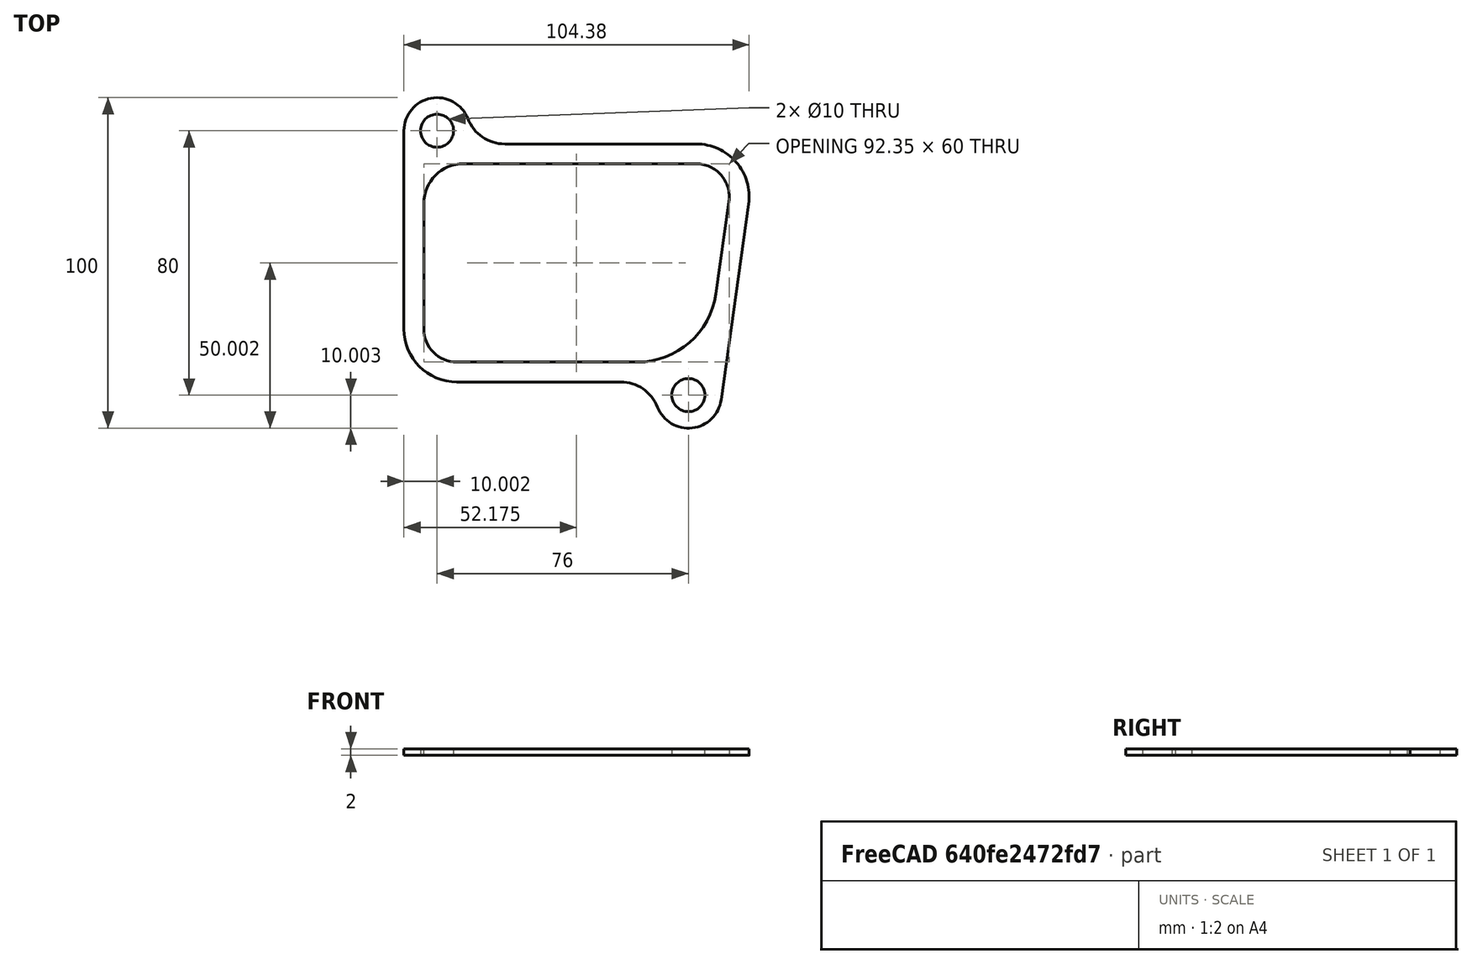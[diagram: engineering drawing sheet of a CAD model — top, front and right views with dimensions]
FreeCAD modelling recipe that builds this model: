
FCSTD DOCUMENT  (FreeCAD 0.20R29410 (Git))
Label: gasket-exercise
License: All rights reserved
LicenseURL: http://en.wikipedia.org/wiki/All_rights_reserved
objects: Sketcher::SketchObject×1, PartDesign::Pad×1, PartDesign::Body×1
note: 4 computed .brp shape members not serialized (recipe doc carries the construction recipe); baked Part::Feature solids carry a one-line shape summary decoded from their .brp

FEATURE [Sketcher::SketchObject] Sketch
  FullyConstrained = false
  MapMode = 5
  Support = -> [XY_Plane]
  sketch-geometry (24):
    g0: Circle CenterX=3.1722 CenterY=-20.9775 CenterZ=0 NormalX=0 NormalY=0 NormalZ=1 AngleXU=0 Radius=5
    g1: Circle CenterX=-72.8278 CenterY=59.0225 CenterZ=0 NormalX=0 NormalY=0 NormalZ=1 AngleXU=0 Radius=5
    g2: LineSegment StartX=-52.3339 StartY=55.0225 StartZ=0 EndX=5.54568 EndY=55.0225 EndZ=0
    g3: ArcOfCircle CenterX=5.54568 CenterY=39.0225 CenterZ=0 NormalX=0 NormalY=0 NormalZ=1 AngleXU=0 Radius=16 StartAngle=6.14356 EndAngle=7.85398
    g4: ArcOfCircle CenterX=3.1722 CenterY=-20.9775 CenterZ=0 NormalX=0 NormalY=0 NormalZ=1 AngleXU=0 Radius=10 StartAngle=3.51376 EndAngle=6.14356
    g5: ArcOfCircle CenterX=-17.3217 CenterY=-28.9775 CenterZ=0 NormalX=0 NormalY=0 NormalZ=1 AngleXU=0 Radius=12 StartAngle=0.372169 EndAngle=1.5708
    g6: LineSegment StartX=-17.3217 StartY=-16.9775 StartZ=0 EndX=-66.8278 EndY=-16.9775 EndZ=0
    g7: ArcOfCircle CenterX=-66.8278 CenterY=-0.977497 CenterZ=0 NormalX=0 NormalY=0 NormalZ=1 AngleXU=0 Radius=16 StartAngle=3.14159 EndAngle=4.71239
    g8: LineSegment StartX=-82.8278 StartY=-0.977497 StartZ=0 EndX=-82.8278 EndY=59.0225 EndZ=0
    g9: ArcOfCircle CenterX=-72.8278 CenterY=59.0225 CenterZ=0 NormalX=0 NormalY=0 NormalZ=1 AngleXU=0 Radius=10 StartAngle=0.372169 EndAngle=3.14159
    g10: ArcOfCircle CenterX=-52.3339 CenterY=67.0225 CenterZ=0 NormalX=0 NormalY=0 NormalZ=1 AngleXU=0 Radius=12 StartAngle=3.51376 EndAngle=4.71239
    g11: LineSegment StartX=13.0749 StartY=-22.3692 StartZ=0 EndX=21.39 EndY=36.7957 EndZ=0
    g12: LineSegment StartX=-64.8278 StartY=49.0225 StartZ=0 EndX=5.54568 EndY=49.0225 EndZ=0
    g13: LineSegment StartX=15.4484 StartY=37.6308 StartZ=0 EndX=11.5205 EndY=9.68235 EndZ=0
    g14: LineSegment StartX=-12.246 StartY=-10.9775 StartZ=0 EndX=-66.8278 EndY=-10.9775 EndZ=0
    g15: LineSegment StartX=-76.8278 StartY=-0.977497 StartZ=0 EndX=-76.8278 EndY=37.0225 EndZ=0
    g16: ArcOfCircle CenterX=5.54568 CenterY=39.0225 CenterZ=0 NormalX=0 NormalY=0 NormalZ=1 AngleXU=0 Radius=10 StartAngle=6.14356 EndAngle=7.85398
    g17: GeomPoint X=17.0494 Y=49.0225 Z=0
    g18: ArcOfCircle CenterX=-12.246 CenterY=13.0225 CenterZ=0 NormalX=0 NormalY=0 NormalZ=1 AngleXU=0 Radius=24 StartAngle=4.71239 EndAngle=6.14356
    g19: GeomPoint X=8.61692 Y=-10.9775 Z=0
    g20: ArcOfCircle CenterX=-64.8278 CenterY=37.0225 CenterZ=0 NormalX=0 NormalY=0 NormalZ=1 AngleXU=0 Radius=12 StartAngle=1.5708 EndAngle=3.14159
    g21: GeomPoint X=-76.8278 Y=49.0225 Z=0
    g22: ArcOfCircle CenterX=-66.8278 CenterY=-0.977497 CenterZ=0 NormalX=0 NormalY=0 NormalZ=1 AngleXU=0 Radius=10 StartAngle=3.14159 EndAngle=4.71239
    g23: GeomPoint X=-76.8278 Y=-10.9775 Z=0
  constraints (54):
    c: Diameter(g0) = 10
    c: Diameter(g1) = 10
    c: DistanceY(g0,g1) = 80
    c: Horizontal(g2)
    c: Tangent(g2,g3) = 1.5708
    c: Tangent(g4,g5) = 1.5708
    c: Tangent(g5,g6) = -1.5708
    c: Tangent(g6,g7) = 1.5708
    c: Tangent(g7,g8) = 1.5708
    c: Tangent(g8,g9) = 1.5708
    c: Tangent(g9,g10) = 1.5708
    c: Tangent(g10,g2) = -1.5708
    c: Horizontal(g6)
    c: Coincident(g9,g1)
    c: Coincident(g4,g0)
    c: Equal(g4,g9)
    c: Radius(g4) = 10
    c: DistanceY(g6,g2) = 72
    c: DistanceX(g7,g0) = 86
    c: Equal(g10,g5)
    c: Radius(g10) = 12
    c: Radius(g3) = 16
    c: Angle(g11,g6) = 1.71042
    c: Tangent(g11,g3) = -1.5708
    c: DistanceY(g0,g5) = 4
    c: Radius(g7) = 16
    c: Tangent(g11,g4) = -1.5708
    c: Horizontal(g12)
    c: Horizontal(g14)
    c: Vertical(g15)
    c: Parallel(g13,g11)
    c: PointOnObject(g17,g12)
    c: PointOnObject(g17,g13)
    c: Tangent(g12,g16) = 1.5708
    c: Tangent(g13,g16) = 1.5708
    c: PointOnObject(g19,g13)
    c: PointOnObject(g19,g14)
    c: Tangent(g13,g18) = 1.5708
    c: Tangent(g14,g18) = 1.5708
    c: PointOnObject(g21,g15)
    c: PointOnObject(g21,g12)
    c: Tangent(g15,g20) = 1.5708
    c: Tangent(g12,g20) = 1.5708
    c: PointOnObject(g23,g14)
    c: PointOnObject(g23,g15)
    c: Tangent(g14,g22) = 1.5708
    c: Tangent(g15,g22) = 1.5708
    c: Radius(g20) = 12
    c: Radius(g18) = 24
    c: Coincident(g16,g3)
    c: Coincident(g22,g7)
    c: Vertical(g8)
    c: Distance(g13,g3) = 6
    c: Distance(g14,g6) = 6
FEATURE [PartDesign::Pad] Pad
  Direction = (0,0,1)
  Length = 2
  Length2 = 10
  Profile = -> Sketch
  ReferenceAxis = -> Sketch [N_Axis]
  Type = 0
FEATURE [PartDesign::Body] Body
  Group = -> [Sketch,Pad]
  Origin = -> Origin
  Tip = -> Pad
